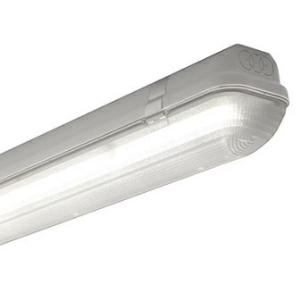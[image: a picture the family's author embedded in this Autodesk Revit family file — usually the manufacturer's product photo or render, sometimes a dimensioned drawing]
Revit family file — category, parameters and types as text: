
# Revit family: 3f_filippi_-_3f_linda_3f_filippi_-_58614_-_3f_linda_led_1x22w_ep_l1570
name_source: partatom
category: Lighting Fixtures
units: mm (PartAtom-declared; Revit-internal decimal feet)

## family parameters
Cut with Voids When Loaded = No
Host = Face
Light Source = No
Part Type = Normal
Room Calculation Point = No
Round Connector Dimension = Use Diameter
Shared = No

## types (1)
- 3F Filippi - 3F Linda (1 x LED, 3955 lm, 26 W, 4000 K)
    Apparent Load = 26 VA
    Approval mark = ENEC
    CIE Flux Codes = 44 77 94 97 100
    Color Rendering = 80
    Color Temperature = 4000 K
    Control Gear = Electronic ballast
    Default Elevation = 1800 mm
    Description = ILLUMINOTECHNICAL
Luminous efficiency 100% (DLOR 97%, ULOR 3%).
Initial luminous flux of the luminaire 3955 lm.
Emergency luminaire luminous flux BLF 15.2%.
Controlled symmetric distribution.
Installation Interdistance Transv.D = 1.77 x hu - Long.D = 1.17 x hu.
Tabular UGR (CIE 117 - 4H-8H; S=0.25H; 70/50/20): RUG 21.1 - 22.1.
Beam angle: 109° - 64°.
Luminous efficacy 152 lm/W.
Lifetime (L93/B10): 30000 h. (tq+25°C)
Lifetime (L90/B10): 50000 h. (tq+25°C)
Lifetime (L85/B10): 80000 h. (tq+25°C)
Lifetime (L80/B10): 100000 h. (tq+25°C)
Sudden decreased luminous flux after 50000 hours: 0% (C0).
Photobiological safety in compliance with IEC/TR 62778: RG0 risk exempt, (IEC 62471).
In compliance with IEC/EN 62722-2-1 - IEC/EN 62717 standards.

SOURCE
Linear LED module 22W/840.
Energy efficiency class (UE 2019/2020 - UE 2019/2015): D.
CIE 13.3 Colour rendering index: CRI >80 (R9 <50%).
IES TM-30 Fidelity Index: Rf = 84 Rg = 95.
CCT nominal colour temperature 4000 K.
Colour initial tolerance (MacAdam): SDCM 3.

MECHANICAL
Self-extinguishing V2 polycarbonate housing, injection moulded, RAL 7035 grey.
Ecologic anti-aging injected sealing gasket.
Diffuser in self-extinguishing V2 polycarbonate, photo-engraved interior, UV stabilised, injection moulded with smooth outer surface, tamper-proof opening.
Gear-holder reflector in hot-dip galvanised steel, painted with white polyester base.
Snug fit safety snap-lock clips for diffuser mounting in stainless steel, screwdriver opening.
Fixing brackets in stainless steel.
Possibility for technicians to access the interior of the luminaire.
Luminaire with limited surface temperature. - D - (EN 60598-2-24)
Dimensions: 1570x100 mm, height 100 mm. Weight 2.81 kg.
IP66 protection degree.
Mechanical strength to impacts IK10 (20 joule).
Glow-wire test resistance 850°C.

ELECTRICAL
Halogen Free electronic wiring 230V-50/60Hz, power factor 0.90, THD <25%, constant output current, SELV, class I, 1 driver.
Power of the luminaire 26 W.
CE - IEC 60598-1 - EN 60598-1.
EP maintained emergency wiring on board, 1h duration, 24h recharge; compliant with EN 60598-2-22, excluding high risk areas.
SAFE FLICKER: PstLM=<1 and SVM=<0.4 (IEC TR 61547-1 and IEC TR 63158), to ensure a more comfortable and safe light.
Ambient temperature from +5°C to +25°C.
Temperature class T6 max 85°C.
Relative humidity UR: <85%.

INSTALLATION
Ceiling / Suspended / Wall.
All accessories dedicated to this product are available on the Catalog and on our website www.3F-Filippi.com.

APPLICATIONS
Suitable product for food production plants (HACCP), IFS (Food Version 6), BRC (GSFS Food Version 7).
Dry, dusty indoor environments, subject to occasional water splashes.
Virtually shatterproof polycarbonate compatibly with the fumes / atmospheres that compromise the elasticity of plastic materials.
Not suitable for installation on surfaces subject to important vibrations, exposed to weather conditions, on ropes or poles.
Suitable for illumination of public car parks and parking grounds referred to DIN 67528:2018-04.

WARNING
Fixture not suitable for cold stores with an ambient temperature <5°C and/or relative humidity >85%.
Luminaire designed for disposal/recycling at end-of-life.
Replaceable (LED only) light source by a professional. Replaceable control gear by a professional.
    Height = 100 mm  [stored 0.328084 ft]
    Lamp = 1 x LED
    Lamp Light Flux = 3955 lm
    Lamp Power = 26 W
    Lamp count = 1
    Length = 1570 mm
    Lifetime = 50000 h
    Luminous efficacy = 152 lm/W
    Manufacturer = 3F Filippi
    ModVariant = No
    Model = 3F Filippi - 58614 - 3F Linda LED 1x22W EP L1570
    Mounting Place = Ceiling
    Mounting Type = Pendant
    Number of Poles = 1
    OnlyDefault = Yes
    Power Factor = 1
    Product Name = 3F Filippi - 3F Linda
    Product group = pendant luminaire
    ProductGroupID = 9
    Protection Class = Protection class I
    Protection Degree = IP 66
    RLX_Detail_Level = 1
    RLX_Emergency_Light_Flux = 0 lm
    RLX_Emergency_Type = 0
    RLX_Emergency_Type_DB = No
    RlxData = <blob elided: 68521 chars, md5=d075d878>
    Socket = socket
    Standby Power = 0 W
    System Light Flux = 3955 lm
    System Power = 26 W
    Type Comments = Product without accessories
    Type Image = 3ffilippi_3f_linda_led_1x.jpg
    URL = http://relux.com
    VarID = ---
    Voltage = 0 V
    Weight = 0.00 kg
    Width = 100 mm  [stored 0.328084 ft]

note: [stored X ft] marks values corroborated as IEEE doubles in the binary element streams (Revit-internal decimal feet)

## geometry (parser evidence)
native form markers: Blend x4, Sweep x10
no freeform markers — native parametric forms only
